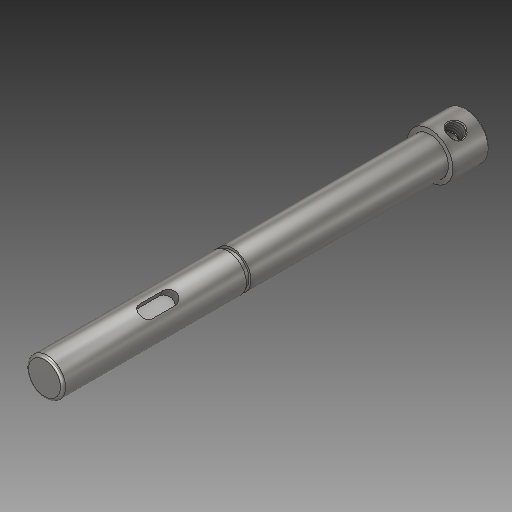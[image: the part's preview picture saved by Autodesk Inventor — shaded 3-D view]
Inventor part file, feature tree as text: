
AUTODESK INVENTOR PART (.ipt)
format: ipt  version: 2019.3 (Build 233278000, 278)  size: 195,584 bytes
history: native  units: mm
features: plane x2, sketch x2, extrude x1, revolve x1, thread x1, fillet x1, chamfer x1, other x1
ambient origin geometry x8: Origin, YZ Plane, XZ Plane, XY Plane, X Axis, Y Axis, Z Axis, Center Point
bodies: Solid1 (feature_tree), Body1 (feature_tree)
feature tree (10):
  plane  "Work Plane1"
  extrude  "Extrusion1"  Depth=2.788mm
  plane  "Work Plane2"
  revolve  "Revolution1"  [1 undecoded]
  thread  "Thread1"  [1 undecoded]
  fillet  "Fillet1"  [1 undecoded]
  chamfer  "Chamfer1"  Angle=90.0deg  [1 undecoded]
  sketch  "Sketch1"  dims[d0=2.0mm d1=2.788mm]
  other  "Work Axis1"
  sketch  "Sketch2"  dims[d2=3.3mm d3=3.0mm d4=0.0mm d5=90.0deg d6=30.0deg d7=90.0deg d8=10.0mm d9=0.0mm d10=0.2mm d11=0.2mm d12=2.0mm d13=45.0deg]
note: 4 required parameter values undecoded (feature->parameter linkage not recoverable at this tier; creation-order binding heuristic only, values carry confidence <= 0.55)